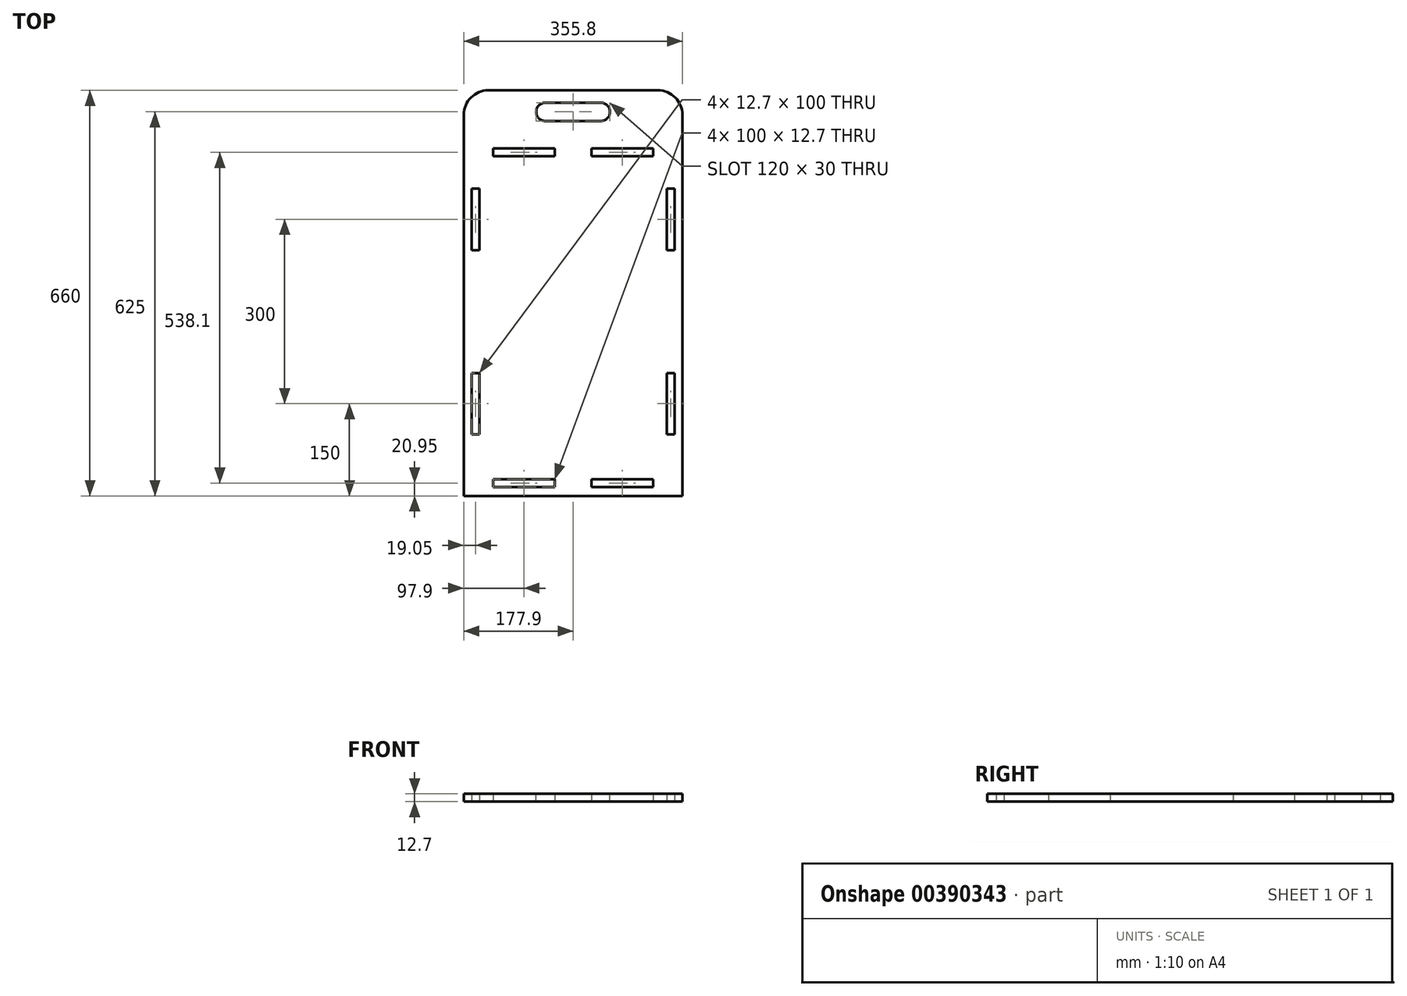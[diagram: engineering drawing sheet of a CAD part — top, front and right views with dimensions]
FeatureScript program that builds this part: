
annotation { "Feature Type Name" : "Feature", "Feature Type Description" : "" }
export const myFeature = defineFeature(function(context is Context, id is Id, definition is map)
    precondition{}
    {
        {
            var Q0;
            Q0=qCreatedBy(makeId("Top.planeOp"),FACE);
            var sketch = newSketch(context, id + "F0", { "sketchPlane" : qUnion([Q0])});
            skLineSegment(sketch, "E0.bottom", {"start": v(177.9, -330) * mm, "end": v(-177.9, -330) * mm});
            skLineSegment(sketch, "E0.top", {"start": v(137.9, 330) * mm, "end": v(-137.9, 330) * mm});
            skLineSegment(sketch, "E0.left", {"start": v(177.9, -330) * mm, "end": v(177.9, 290) * mm});
            skLineSegment(sketch, "E0.right", {"start": v(-177.9, -330) * mm, "end": v(-177.9, 290) * mm});
            skPoint(sketch, "E0.middle", {"position": v(0, 0) * mm});
            skPoint(sketch, "E1.visualSharp", {"position": v(-177.9, 330) * mm});
            skArc(sketch, "E1.filletArc", {"start": v(-137.9, 330) * mm, "mid": v(-166.18, 318.28) * mm, "end": v(-177.9, 290) * mm});
            skPoint(sketch, "E2.visualSharp", {"position": v(177.9, 330) * mm});
            skArc(sketch, "E2.filletArc", {"start": v(177.9, 290) * mm, "mid": v(166.18, 318.28) * mm, "end": v(137.9, 330) * mm});
            skLineSegment(sketch, "E3", {"start": v(-177.9, -30) * mm, "end": v(177.9, -30) * mm, "construction": true});
            skLineSegment(sketch, "E4", {"start": v(-165.2, -30) * mm, "end": v(-165.2, -330) * mm, "construction": true});
            skLineSegment(sketch, "E5", {"start": v(-165.2, -130) * mm, "end": v(177.9, -130) * mm, "construction": true});
            skLineSegment(sketch, "E6.bottom", {"start": v(-165.2, -130) * mm, "end": v(-152.5, -130) * mm});
            skLineSegment(sketch, "E6.top", {"start": v(-165.2, -230) * mm, "end": v(-152.5, -230) * mm});
            skLineSegment(sketch, "E6.left", {"start": v(-165.2, -130) * mm, "end": v(-165.2, -230) * mm});
            skLineSegment(sketch, "E6.right", {"start": v(-152.5, -130) * mm, "end": v(-152.5, -230) * mm});
            skLineSegment(sketch, "E7.MirrorCS", {"start": v(-165.2, 170) * mm, "end": v(-152.5, 170) * mm});
            skLineSegment(sketch, "E8.MirrorCS", {"start": v(-165.2, 70) * mm, "end": v(-152.5, 70) * mm});
            skLineSegment(sketch, "E9.MirrorCS", {"start": v(-152.5, 70) * mm, "end": v(-152.5, 170) * mm});
            skLineSegment(sketch, "E10.MirrorCS", {"start": v(-165.2, 70) * mm, "end": v(-165.2, 170) * mm});
            skLineSegment(sketch, "E11.MirrorCS", {"start": v(165.2, -230) * mm, "end": v(152.5, -230) * mm});
            skLineSegment(sketch, "E12.MirrorCS", {"start": v(165.2, -130) * mm, "end": v(152.5, -130) * mm});
            skLineSegment(sketch, "E13.MirrorCS", {"start": v(165.2, -130) * mm, "end": v(165.2, -230) * mm});
            skLineSegment(sketch, "E14.MirrorCS", {"start": v(152.5, -130) * mm, "end": v(152.5, -230) * mm});
            skLineSegment(sketch, "E15.MirrorCS", {"start": v(165.2, 70) * mm, "end": v(165.2, 170) * mm});
            skLineSegment(sketch, "E16.MirrorCS", {"start": v(165.2, 170) * mm, "end": v(152.5, 170) * mm});
            skLineSegment(sketch, "E17.MirrorCS", {"start": v(152.5, 70) * mm, "end": v(152.5, 170) * mm});
            skLineSegment(sketch, "E18.MirrorCS", {"start": v(165.2, 70) * mm, "end": v(152.5, 70) * mm});
            skLineSegment(sketch, "E19", {"start": v(-177.9, 222.7) * mm, "end": v(177.9, 222.7) * mm, "construction": true});
            skLineSegment(sketch, "E20.bottom", {"start": v(-130, 222.7) * mm, "end": v(-30, 222.7) * mm});
            skLineSegment(sketch, "E20.top", {"start": v(-130, 235.4) * mm, "end": v(-30, 235.4) * mm});
            skLineSegment(sketch, "E20.left", {"start": v(-130, 222.7) * mm, "end": v(-130, 235.4) * mm});
            skLineSegment(sketch, "E20.right", {"start": v(-30, 222.7) * mm, "end": v(-30, 235.4) * mm});
            skLineSegment(sketch, "E21.MirrorCS", {"start": v(130, 222.7) * mm, "end": v(130, 235.4) * mm});
            skLineSegment(sketch, "E22.MirrorCS", {"start": v(30, 222.7) * mm, "end": v(30, 235.4) * mm});
            skLineSegment(sketch, "E23.MirrorCS", {"start": v(130, 235.4) * mm, "end": v(30, 235.4) * mm});
            skLineSegment(sketch, "E24.MirrorCS", {"start": v(130, 222.7) * mm, "end": v(30, 222.7) * mm});
            skLineSegment(sketch, "E25", {"start": v(-177.9, -302.7) * mm, "end": v(177.9, -302.7) * mm, "construction": true});
            skLineSegment(sketch, "E26.bottom", {"start": v(-130, -302.7) * mm, "end": v(-30, -302.7) * mm});
            skLineSegment(sketch, "E26.top", {"start": v(-130, -315.4) * mm, "end": v(-30, -315.4) * mm});
            skLineSegment(sketch, "E26.left", {"start": v(-130, -302.7) * mm, "end": v(-130, -315.4) * mm});
            skLineSegment(sketch, "E26.right", {"start": v(-30, -302.7) * mm, "end": v(-30, -315.4) * mm});
            skLineSegment(sketch, "E27.MirrorCS", {"start": v(130, -302.7) * mm, "end": v(30, -302.7) * mm});
            skLineSegment(sketch, "E28.MirrorCS", {"start": v(30, -302.7) * mm, "end": v(30, -315.4) * mm});
            skLineSegment(sketch, "E29.MirrorCS", {"start": v(130, -302.7) * mm, "end": v(130, -315.4) * mm});
            skLineSegment(sketch, "E30.MirrorCS", {"start": v(130, -315.4) * mm, "end": v(30, -315.4) * mm});
            skSolve(sketch);
        }
        {
            var Q0;
            Q0 = qSketchRegion(id + "F0", true);
            extrude(context, id + "F1", {"entities" : qUnion([Q0]), "depth" : 12.7 * mm});
        }
        {
            var Q0;
            Q0=makeQuery(id+"F1.opExtrude","CAP_FACE",FACE,{"disambiguationData":[OSD([sQuery(id+"F0.wireOp",EDGE,"E0.bottom"),sQuery(id+"F0.wireOp",EDGE,"E0.top"),sQuery(id+"F0.wireOp",EDGE,"E0.left"),sQuery(id+"F0.wireOp",EDGE,"E0.right"),sQuery(id+"F0.wireOp",EDGE,"E1.filletArc"),sQuery(id+"F0.wireOp",EDGE,"E2.filletArc"),sQuery(id+"F0.wireOp",EDGE,"E6.bottom"),sQuery(id+"F0.wireOp",EDGE,"E6.top"),sQuery(id+"F0.wireOp",EDGE,"E6.left"),sQuery(id+"F0.wireOp",EDGE,"E6.right"),sQuery(id+"F0.wireOp",EDGE,"E7.MirrorCS"),sQuery(id+"F0.wireOp",EDGE,"E8.MirrorCS"),sQuery(id+"F0.wireOp",EDGE,"E9.MirrorCS"),sQuery(id+"F0.wireOp",EDGE,"E10.MirrorCS"),sQuery(id+"F0.wireOp",EDGE,"E11.MirrorCS"),sQuery(id+"F0.wireOp",EDGE,"E12.MirrorCS"),sQuery(id+"F0.wireOp",EDGE,"E13.MirrorCS"),sQuery(id+"F0.wireOp",EDGE,"E14.MirrorCS"),sQuery(id+"F0.wireOp",EDGE,"E15.MirrorCS"),sQuery(id+"F0.wireOp",EDGE,"E16.MirrorCS"),sQuery(id+"F0.wireOp",EDGE,"E17.MirrorCS"),sQuery(id+"F0.wireOp",EDGE,"E18.MirrorCS"),sQuery(id+"F0.wireOp",EDGE,"E20.bottom"),sQuery(id+"F0.wireOp",EDGE,"E20.top"),sQuery(id+"F0.wireOp",EDGE,"E20.left"),sQuery(id+"F0.wireOp",EDGE,"E20.right"),sQuery(id+"F0.wireOp",EDGE,"E21.MirrorCS"),sQuery(id+"F0.wireOp",EDGE,"E22.MirrorCS"),sQuery(id+"F0.wireOp",EDGE,"E23.MirrorCS"),sQuery(id+"F0.wireOp",EDGE,"E24.MirrorCS"),sQuery(id+"F0.wireOp",EDGE,"E26.bottom"),sQuery(id+"F0.wireOp",EDGE,"E26.top"),sQuery(id+"F0.wireOp",EDGE,"E26.left"),sQuery(id+"F0.wireOp",EDGE,"E26.right"),sQuery(id+"F0.wireOp",EDGE,"E27.MirrorCS"),sQuery(id+"F0.wireOp",EDGE,"E28.MirrorCS"),sQuery(id+"F0.wireOp",EDGE,"E29.MirrorCS"),sQuery(id+"F0.wireOp",EDGE,"E30.MirrorCS")])],"isStart":false});
            var sketch = newSketch(context, id + "F2", { "sketchPlane" : qUnion([Q0])});
            skLineSegment(sketch, "E31.bottom", {"start": v(-45, 280) * mm, "end": v(45, 280) * mm});
            skLineSegment(sketch, "E31.top", {"start": v(-45, 310) * mm, "end": v(45, 310) * mm});
            skLineSegment(sketch, "E31.left", {"start": v(-60, 295) * mm, "end": v(-60, 295) * mm});
            skLineSegment(sketch, "E31.right", {"start": v(60, 295) * mm, "end": v(60, 295) * mm});
            skPoint(sketch, "E31.middle", {"position": v(0, 295) * mm});
            skPoint(sketch, "E32.visualSharp", {"position": v(-60, 310) * mm});
            skArc(sketch, "E32.filletArc", {"start": v(-45, 310) * mm, "mid": v(-55.6, 305.6) * mm, "end": v(-60, 295) * mm});
            skPoint(sketch, "E33.visualSharp", {"position": v(60, 310) * mm});
            skArc(sketch, "E33.filletArc", {"start": v(60, 295) * mm, "mid": v(55.6, 305.6) * mm, "end": v(45, 310) * mm});
            skPoint(sketch, "E34.visualSharp", {"position": v(-60, 280) * mm});
            skArc(sketch, "E34.filletArc", {"start": v(-60, 295) * mm, "mid": v(-55.6, 284.4) * mm, "end": v(-45, 280) * mm});
            skPoint(sketch, "E35.visualSharp", {"position": v(60, 280) * mm});
            skArc(sketch, "E35.filletArc", {"start": v(45, 280) * mm, "mid": v(55.6, 284.4) * mm, "end": v(60, 295) * mm});
            skSolve(sketch);
        }
        {
            var Q0;
            Q0 = qSketchRegion(id + "F2", true);
            extrude(context, id + "F3", {"entities" : qUnion([Q0]), "operationType" : NewBodyOperationType.REMOVE, "endBound" : BoundingType.UP_TO_NEXT, "oppositeDirection" : true, "depth" : 25 * mm});
        }
    });
